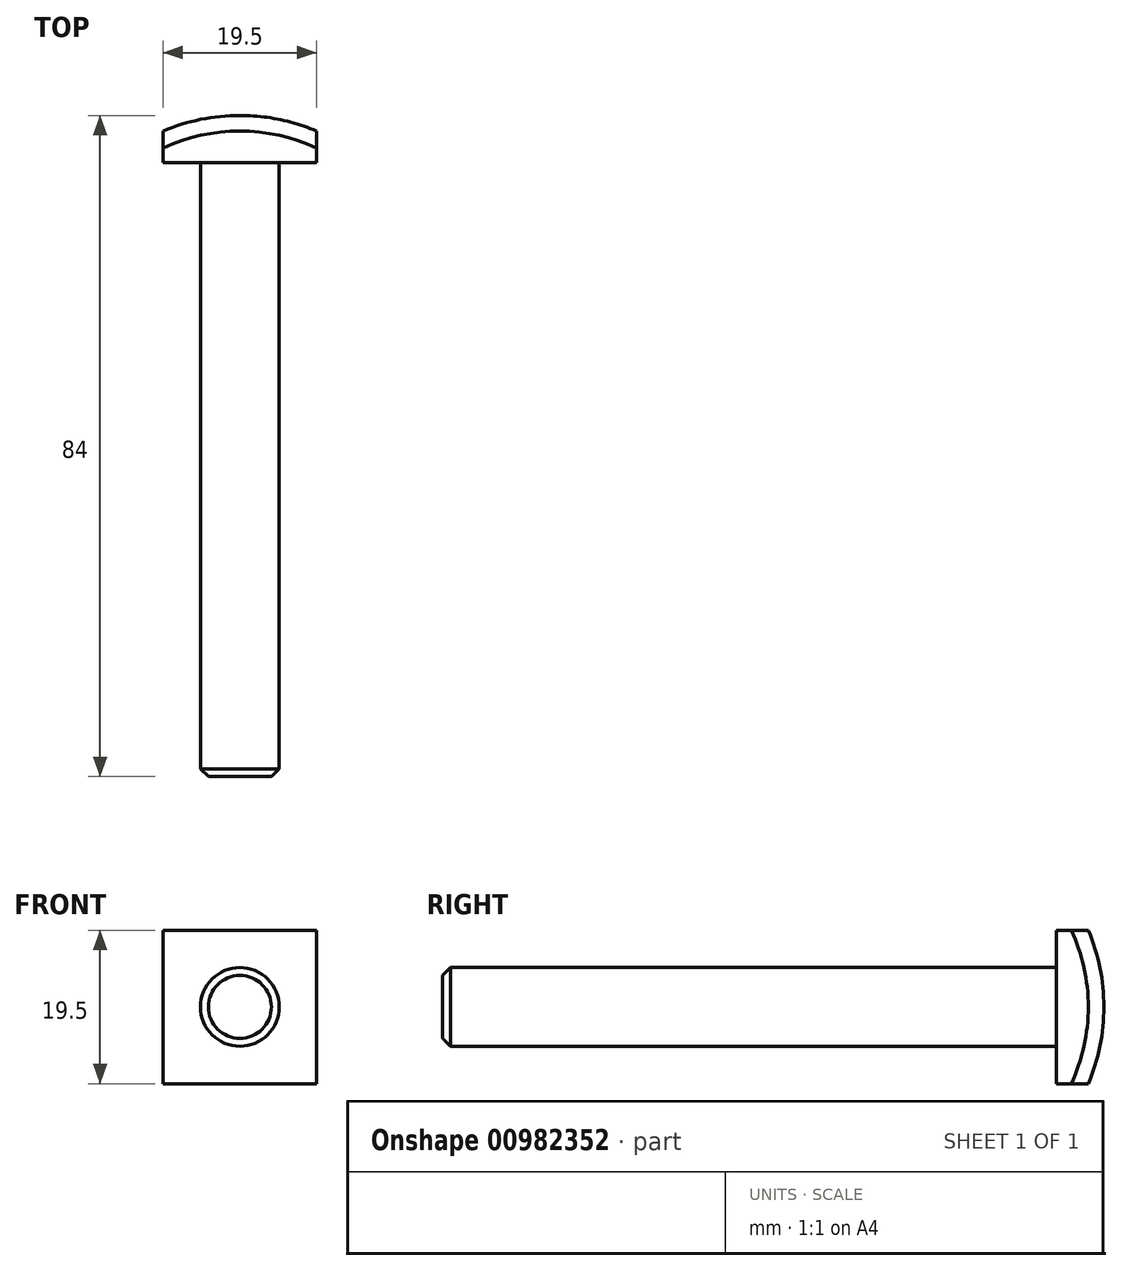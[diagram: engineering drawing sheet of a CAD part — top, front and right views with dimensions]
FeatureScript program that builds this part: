
annotation { "Feature Type Name" : "Feature", "Feature Type Description" : "" }
export const myFeature = defineFeature(function(context is Context, id is Id, definition is map)
    precondition{}
    {
        {
            var Q0;
            Q0=qCreatedBy(makeId("Front.planeOp"),FACE);
            var sketch = newSketch(context, id + "F0", { "sketchPlane" : qUnion([Q0])});
            skLineSegment(sketch, "E0.bottom", {"start": v(9.75, 9.75) * mm, "end": v(-9.75, 9.75) * mm});
            skLineSegment(sketch, "E0.top", {"start": v(9.75, -9.75) * mm, "end": v(-9.75, -9.75) * mm});
            skLineSegment(sketch, "E0.left", {"start": v(9.75, 9.75) * mm, "end": v(9.75, -9.75) * mm});
            skLineSegment(sketch, "E0.right", {"start": v(-9.75, 9.75) * mm, "end": v(-9.75, -9.75) * mm});
            skPoint(sketch, "E0.middle", {"position": v(0, 0) * mm});
            skLineSegment(sketch, "E1", {"start": v(-9.75, 9.75) * mm, "end": v(9.75, -9.75) * mm, "construction": true});
            skLineSegment(sketch, "E2", {"start": v(9.75, 9.75) * mm, "end": v(-9.75, -9.75) * mm, "construction": true});
            skSolve(sketch);
        }
        {
            var Q0;
            Q0=qSketchRegion(id+"F0",true);
            extrude(context, id + "F1", {"entities" : qUnion([Q0]), "depth" : 6 * mm, "offsetDistance" : 25 * mm});
        }
        {
            var Q0;
            Q0=makeQuery(id+"F1.opExtrude","CAP_FACE",FACE,{"disambiguationData":[OSD([sQuery(id+"F0.wireOp",EDGE,"E0.bottom"),sQuery(id+"F0.wireOp",EDGE,"E0.top"),sQuery(id+"F0.wireOp",EDGE,"E0.left"),sQuery(id+"F0.wireOp",EDGE,"E0.right")])],"isStart":false});
            var sketch = newSketch(context, id + "F2", { "sketchPlane" : qUnion([Q0])});
            skCircle(sketch, "E3", {"center": v(0, 0) * mm, "radius": 5 * mm});
            skSolve(sketch);
        }
        {
            var Q0;
            Q0=qSketchRegion(id+"F2",true);
            extrude(context, id + "F3", {"entities" : qUnion([Q0]), "operationType" : NewBodyOperationType.ADD, "depth" : 78 * mm, "offsetDistance" : 25 * mm});
        }
        {
            var Q0;
            Q0=makeQuery(id+"F3.opExtrude","CAP_FACE",FACE,{"disambiguationData":[OSD([sQuery(id+"F2.wireOp",EDGE,"E3")])],"isStart":false});
            chamfer(context, id + "F4", {"entities" : qUnion([Q0]), "width" : 1 * mm, "tangentPropagation" : true});
        }
        {
            var Q0;
            Q0=qCreatedBy(makeId("Top.planeOp"),FACE);
            var sketch = newSketch(context, id + "F5", { "sketchPlane" : qUnion([Q0])});
            skArc(sketch, "E4", {"start": v(25, -25) * mm, "mid": v(17.68, -7.32) * mm, "end": v(0, 0) * mm});
            skArc(sketch, "E5", {"start": v(35.53, -25) * mm, "mid": v(25.12, 0.12) * mm, "end": v(0, 10.53) * mm});
            skLineSegment(sketch, "E6", {"start": v(0, 10.53) * mm, "end": v(0, 0) * mm});
            skLineSegment(sketch, "E7", {"start": v(25, -25) * mm, "end": v(35.53, -25) * mm});
            skSolve(sketch);
        }
        {
            var Q0;
            Q0=qSketchRegion(id+"F5",true);
            var Q1;
            Q1=sQuery(id+"F5.wireOp",EDGE,"E6");
            revolve(context, id + "F6", {"operationType" : NewBodyOperationType.REMOVE, "surfaceOperationType" : NewSurfaceOperationType.NEW, "entities" : qUnion([Q0]), "axis" : qUnion([Q1]), "revolveType" : RevolveType.FULL, "oppositeDirection" : true});
        }
    });
